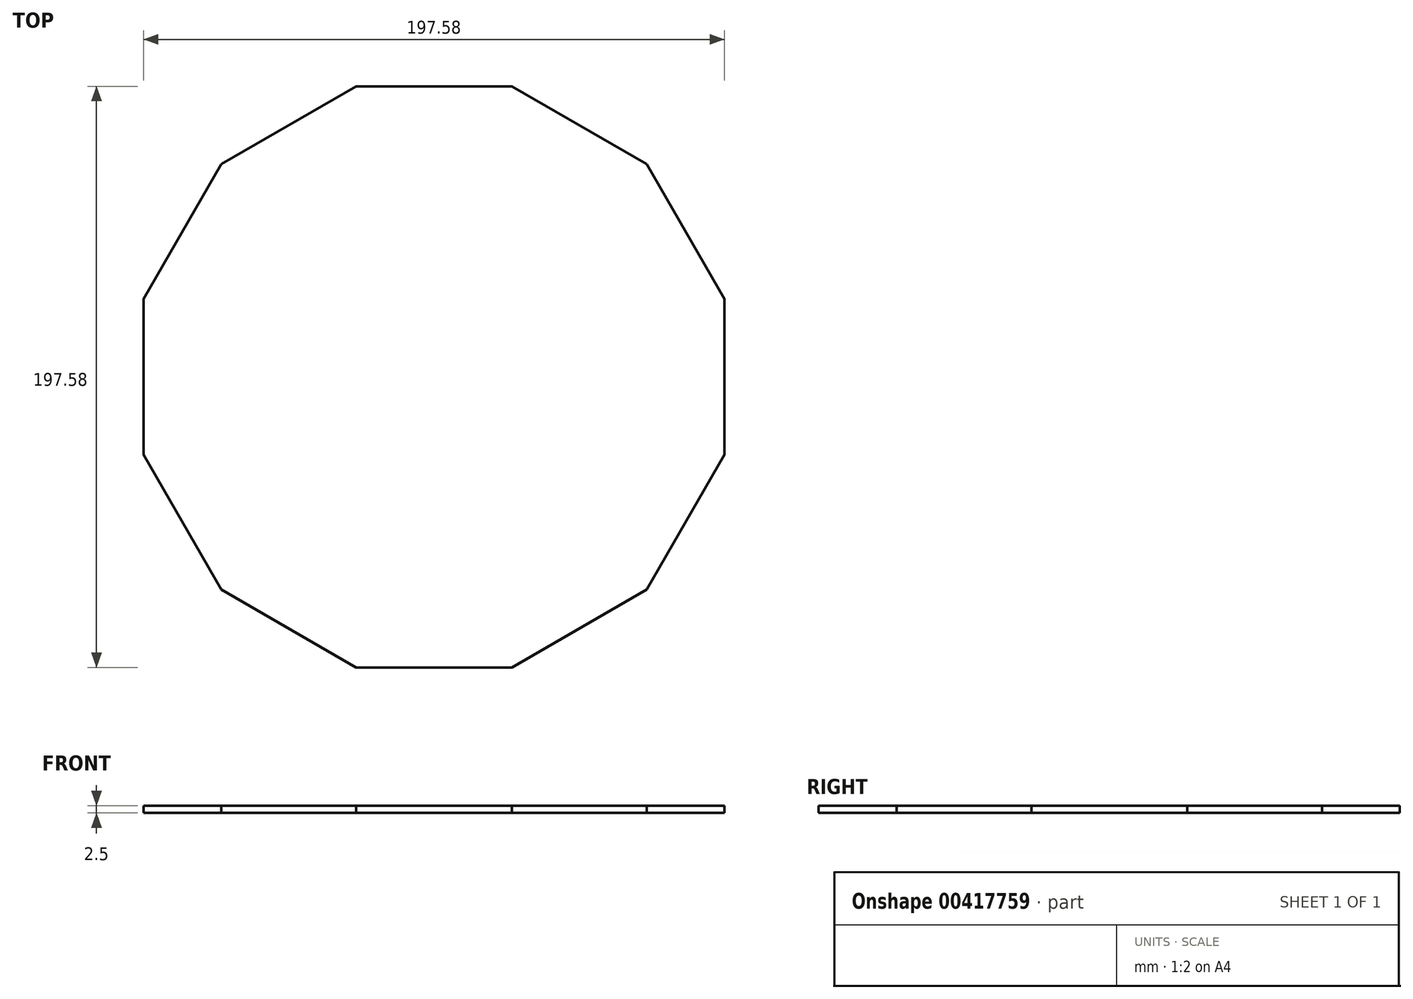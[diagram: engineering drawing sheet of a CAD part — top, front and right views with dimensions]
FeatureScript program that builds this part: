
annotation { "Feature Type Name" : "Feature", "Feature Type Description" : "" }
export const myFeature = defineFeature(function(context is Context, id is Id, definition is map)
    precondition{}
    {
        {
            var Q0;
            Q0=qCreatedBy(makeId("Top.planeOp"),FACE);
            var sketch = newSketch(context, id + "F0", { "sketchPlane" : qUnion([Q0])});
            skCircle(sketch, "E0.cCircle", {"center": v(0, 0) * mm, "radius": 98.79 * mm, "construction": true});
            skLineSegment(sketch, "E0.0", {"start": v(-98.79, -26.47) * mm, "end": v(-98.79, 26.47) * mm});
            skLineSegment(sketch, "E0.1", {"start": v(-98.79, 26.47) * mm, "end": v(-72.32, 72.32) * mm});
            skLineSegment(sketch, "E0.2", {"start": v(-72.32, 72.32) * mm, "end": v(-26.47, 98.79) * mm});
            skLineSegment(sketch, "E0.3", {"start": v(-26.47, 98.79) * mm, "end": v(26.47, 98.79) * mm});
            skLineSegment(sketch, "E0.4", {"start": v(26.47, 98.79) * mm, "end": v(72.32, 72.32) * mm});
            skLineSegment(sketch, "E0.5", {"start": v(72.32, 72.32) * mm, "end": v(98.79, 26.47) * mm});
            skLineSegment(sketch, "E0.6", {"start": v(98.79, 26.47) * mm, "end": v(98.79, -26.47) * mm});
            skLineSegment(sketch, "E0.7", {"start": v(98.79, -26.47) * mm, "end": v(72.32, -72.32) * mm});
            skLineSegment(sketch, "E0.8", {"start": v(72.32, -72.32) * mm, "end": v(26.47, -98.79) * mm});
            skLineSegment(sketch, "E0.9", {"start": v(26.47, -98.79) * mm, "end": v(-26.47, -98.79) * mm});
            skLineSegment(sketch, "E0.10", {"start": v(-26.47, -98.79) * mm, "end": v(-72.32, -72.32) * mm});
            skLineSegment(sketch, "E0.11", {"start": v(-72.32, -72.32) * mm, "end": v(-98.79, -26.47) * mm});
            skPoint(sketch, "E0.0.midPoint", {"position": v(-98.79, 0) * mm});
            skSolve(sketch);
        }
        {
            var Q0;
            Q0=makeQuery(id+"F0.imprint","IMPRINT",FACE,{"disambiguationData":[TD([[makeQuery(id+"F0.imprint","IMPRINT",EDGE,{"derivedFrom":sQuery(id+"F0.wireOp",EDGE,"E0.0")}),-1.0]])]});
            extrude(context, id + "F1", {"entities" : qUnion([Q0]), "depth" : 2.5 * mm});
        }
    });
